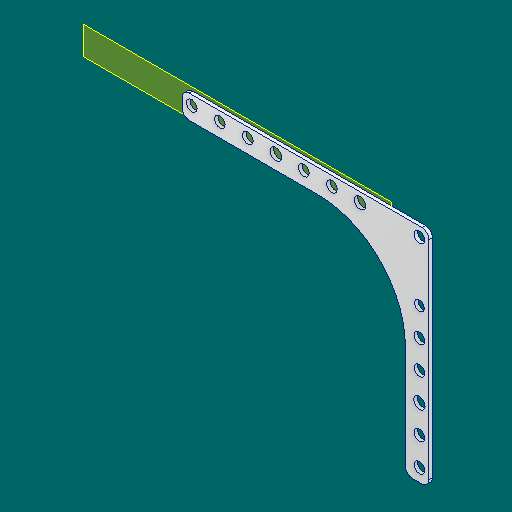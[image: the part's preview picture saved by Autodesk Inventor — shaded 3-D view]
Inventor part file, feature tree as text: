
AUTODESK INVENTOR PART (.ipt)
format: ipt  version: 2023.1 (Build 271208000, 208)  size: 147,968 bytes
history: native  units: in
note: dims shown in document units (in); Inventor stores cm internally (conversion verified against a paired STEP export)
features: other x3, sketch x1, plane x1
ambient origin geometry x8: Origin, YZ Plane, XZ Plane, XY Plane, X Axis, Y Axis, Z Axis, Center Point
bodies: Solid1 (feature_tree)
feature tree (5):
  other  "UnderGusset_MIR.ipt"
  other  "Solid1::UnderGusset_MIR.ipt"
  other  "TaggingFeature1"
  sketch  "Sketch1"  dims[d0=0.3937in]
  plane  "Work Plane1"
